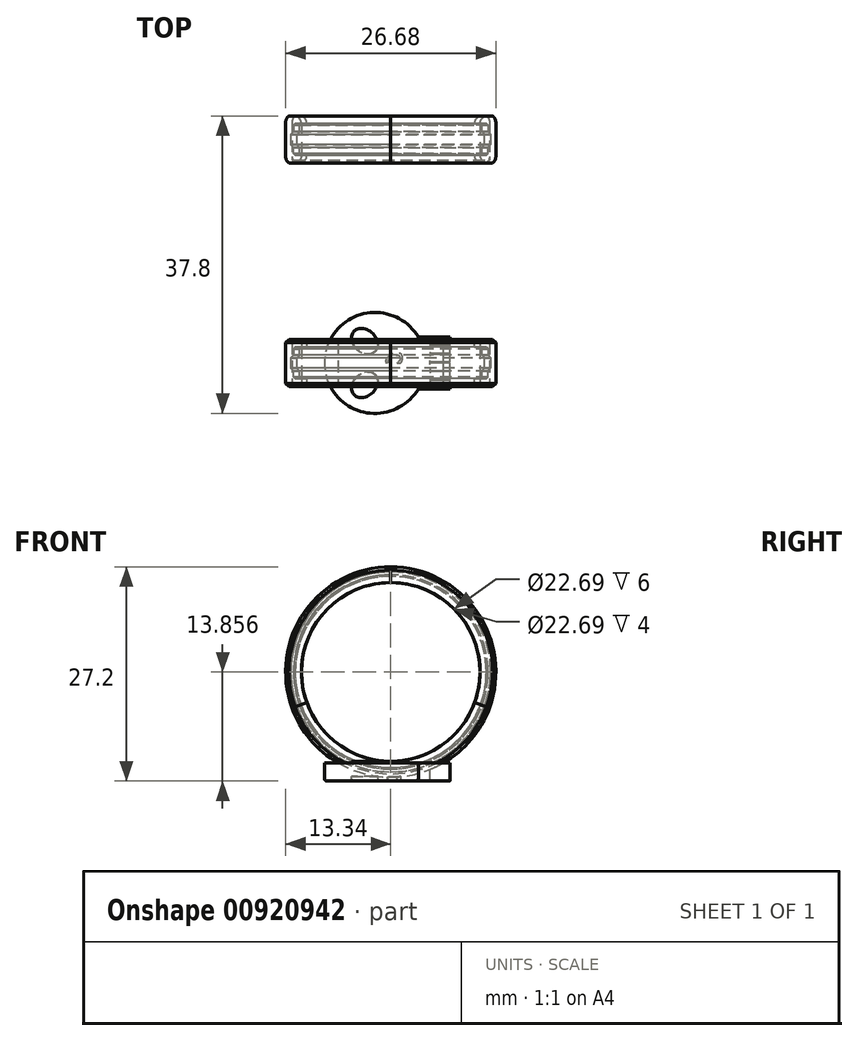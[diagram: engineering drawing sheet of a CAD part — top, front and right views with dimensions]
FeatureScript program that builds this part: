
annotation { "Feature Type Name" : "Feature", "Feature Type Description" : "" }
export const myFeature = defineFeature(function(context is Context, id is Id, definition is map)
    precondition{}
    {
        {
            var Q0;
            Q0=qCreatedBy(makeId("Right.planeOp"),FACE);
            var sketch = newSketch(context, id + "F0", { "sketchPlane" : qUnion([Q0])});
            skLineSegment(sketch, "E0", {"start": v(-19.63, -18.34) * mm, "end": v(80.37, -18.34) * mm, "construction": true});
            skLineSegment(sketch, "E1", {"start": v(-43.65, -18.34) * mm, "end": v(56.35, -18.34) * mm, "construction": true});
            skLineSegment(sketch, "E2.left", {"start": v(-31.4, -5.4) * mm, "end": v(-31.4, -7) * mm});
            skLineSegment(sketch, "E3", {"start": v(-30.2, -6) * mm, "end": v(-29.4, -6) * mm});
            skLineSegment(sketch, "E4", {"start": v(-27.4, -6) * mm, "end": v(-26.6, -6) * mm});
            skLineSegment(sketch, "E5", {"start": v(-29.4, -6) * mm, "end": v(-29.05, -5.65) * mm});
            skLineSegment(sketch, "E6", {"start": v(-27.4, -6) * mm, "end": v(-27.75, -5.65) * mm});
            skLineSegment(sketch, "E7", {"start": v(-30.4, -6.2) * mm, "end": v(-30.4, -7) * mm});
            skLineSegment(sketch, "E8", {"start": v(-26.4, -6.2) * mm, "end": v(-26.4, -7) * mm});
            skLineSegment(sketch, "E9", {"start": v(-31.4, -7) * mm, "end": v(-30.4, -7) * mm});
            skLineSegment(sketch, "E10", {"start": v(-26.4, -7) * mm, "end": v(-25.4, -7) * mm});
            skLineSegment(sketch, "E11", {"start": v(-30.4, -7) * mm, "end": v(-26.4, -7) * mm});
            skLineSegment(sketch, "E12", {"start": v(-29.05, -5.65) * mm, "end": v(-27.75, -5.65) * mm});
            skLineSegment(sketch, "E13", {"start": v(-25.4, -7) * mm, "end": v(-25.4, -5.4) * mm});
            skLineSegment(sketch, "E14", {"start": v(-25.8, -5) * mm, "end": v(-31, -5) * mm});
            skLineSegment(sketch, "E15", {"start": v(-31, -5) * mm, "end": v(-31.4, -5.4) * mm});
            skLineSegment(sketch, "E16", {"start": v(-25.4, -5.4) * mm, "end": v(-25.8, -5) * mm});
            skLineSegment(sketch, "E17", {"start": v(-30.4, -6.2) * mm, "end": v(-30.2, -6) * mm});
            skLineSegment(sketch, "E18", {"start": v(-26.4, -6.2) * mm, "end": v(-26.6, -6) * mm});
            skPoint(sketch, "E19.orphan", {"position": v(-31.4, -5) * mm});
            skPoint(sketch, "E20.orphan", {"position": v(-26.4, -6) * mm});
            skPoint(sketch, "E21.orphan", {"position": v(-30.4, -6) * mm});
            skLineSegment(sketch, "E22.left", {"start": v(-3.01, -5.4) * mm, "end": v(-3, -7) * mm});
            skLineSegment(sketch, "E23", {"start": v(-1.81, -6) * mm, "end": v(-1.01, -6) * mm});
            skLineSegment(sketch, "E24", {"start": v(1, -6) * mm, "end": v(1.8, -6) * mm});
            skLineSegment(sketch, "E25", {"start": v(-1.01, -6) * mm, "end": v(-0.66, -5.65) * mm});
            skLineSegment(sketch, "E26", {"start": v(1, -6) * mm, "end": v(0.64, -5.65) * mm});
            skLineSegment(sketch, "E27", {"start": v(-2.01, -6.2) * mm, "end": v(-2, -7) * mm});
            skLineSegment(sketch, "E28", {"start": v(2, -6.2) * mm, "end": v(2, -7) * mm});
            skLineSegment(sketch, "E29", {"start": v(-3, -7) * mm, "end": v(-2, -7) * mm});
            skLineSegment(sketch, "E30", {"start": v(2, -7) * mm, "end": v(3, -7) * mm});
            skLineSegment(sketch, "E31", {"start": v(-2, -7) * mm, "end": v(2, -7) * mm});
            skLineSegment(sketch, "E32", {"start": v(-0.66, -5.65) * mm, "end": v(0.64, -5.65) * mm});
            skLineSegment(sketch, "E33", {"start": v(3, -7) * mm, "end": v(3, -5.4) * mm});
            skLineSegment(sketch, "E34", {"start": v(2.6, -5) * mm, "end": v(-2.61, -5) * mm});
            skLineSegment(sketch, "E35", {"start": v(-2.61, -5) * mm, "end": v(-3.01, -5.4) * mm});
            skLineSegment(sketch, "E36", {"start": v(3, -5.4) * mm, "end": v(2.6, -5) * mm});
            skLineSegment(sketch, "E37", {"start": v(-2.01, -6.2) * mm, "end": v(-1.81, -6) * mm});
            skLineSegment(sketch, "E38", {"start": v(2, -6.2) * mm, "end": v(1.8, -6) * mm});
            skPoint(sketch, "E39.orphan", {"position": v(-3.01, -5) * mm});
            skPoint(sketch, "E40.orphan", {"position": v(2, -6) * mm});
            skPoint(sketch, "E41.orphan", {"position": v(-2.01, -6) * mm});
            skSolve(sketch);
        }
        {
            var Q0;
            Q0=makeQuery(id+"F0.imprint","IMPRINT",FACE,{"disambiguationData":[TD([[makeQuery(id+"F0.imprint","IMPRINT",EDGE,{"derivedFrom":sQuery(id+"F0.wireOp",EDGE,"E3")}),-1.0]])]});
            var Q1;
            Q1=makeQuery(id+"F0.imprint","IMPRINT",FACE,{"disambiguationData":[TD([[makeQuery(id+"F0.imprint","IMPRINT",EDGE,{"derivedFrom":sQuery(id+"F0.wireOp",EDGE,"E23")}),-1.0]])]});
            var Q2;
            Q2=sQuery(id+"F0.wireOp",EDGE,"E0");
            revolve(context, id + "F1", {"surfaceOperationType" : NewSurfaceOperationType.NEW, "entities" : qUnion([Q0, Q1]), "axis" : qUnion([Q2]), "revolveType" : RevolveType.FULL});
        }
        {
            var Q0;
            Q0=makeQuery(id+"F0.imprint","IMPRINT",FACE,{"disambiguationData":[TD([[makeQuery(id+"F0.imprint","IMPRINT",EDGE,{"derivedFrom":sQuery(id+"F0.wireOp",EDGE,"E2.left")}),1.0]])]});
            var Q1;
            Q1=makeQuery(id+"F0.imprint","IMPRINT",FACE,{"disambiguationData":[TD([[makeQuery(id+"F0.imprint","IMPRINT",EDGE,{"derivedFrom":sQuery(id+"F0.wireOp",EDGE,"E22.left")}),1.0]])]});
            var Q2;
            Q2=sQuery(id+"F0.wireOp",EDGE,"E0");
            revolve(context, id + "F2", {"surfaceOperationType" : NewSurfaceOperationType.NEW, "entities" : qUnion([Q0, Q1]), "axis" : qUnion([Q2]), "revolveType" : RevolveType.ONE_DIRECTION, "angle" : 110 * degree});
        }
        {
            var Q0;
            Q0=makeQuery(id+"F0.imprint","IMPRINT",FACE,{"disambiguationData":[TD([[makeQuery(id+"F0.imprint","IMPRINT",EDGE,{"derivedFrom":sQuery(id+"F0.wireOp",EDGE,"E2.left")}),1.0]])]});
            var Q1;
            Q1=makeQuery(id+"F0.imprint","IMPRINT",FACE,{"disambiguationData":[TD([[makeQuery(id+"F0.imprint","IMPRINT",EDGE,{"derivedFrom":sQuery(id+"F0.wireOp",EDGE,"E22.left")}),1.0]])]});
            var Q2;
            Q2=sQuery(id+"F0.wireOp",EDGE,"E0");
            revolve(context, id + "F3", {"surfaceOperationType" : NewSurfaceOperationType.NEW, "entities" : qUnion([Q0, Q1]), "axis" : qUnion([Q2]), "revolveType" : RevolveType.TWO_DIRECTIONS, "angle" : 250 * degree, "angleBack" : 110 * degree});
        }
        {
            var Q0;
            Q0=makeQuery(id+"F0.imprint","IMPRINT",FACE,{"disambiguationData":[TD([[makeQuery(id+"F0.imprint","IMPRINT",EDGE,{"derivedFrom":sQuery(id+"F0.wireOp",EDGE,"E2.left")}),1.0]])]});
            var Q1;
            Q1=makeQuery(id+"F0.imprint","IMPRINT",FACE,{"disambiguationData":[TD([[makeQuery(id+"F0.imprint","IMPRINT",EDGE,{"derivedFrom":sQuery(id+"F0.wireOp",EDGE,"E22.left")}),1.0]])]});
            var Q2;
            Q2=sQuery(id+"F0.wireOp",EDGE,"E0");
            revolve(context, id + "F4", {"surfaceOperationType" : NewSurfaceOperationType.NEW, "entities" : qUnion([Q0, Q1]), "axis" : qUnion([Q2]), "revolveType" : RevolveType.TWO_DIRECTIONS, "angle" : 360 * degree, "angleBack" : 250 * degree});
        }
        {
            var Q0;
            Q0=qCreatedBy(makeId("Top.planeOp"),FACE);
            var sketch = newSketch(context, id + "F5", { "sketchPlane" : qUnion([Q0])});
            skLineSegment(sketch, "E42.bottom", {"start": v(-7.5, -35.4) * mm, "end": v(7.5, -35.4) * mm, "construction": true});
            skLineSegment(sketch, "E42.top", {"start": v(-7.5, -21.4) * mm, "end": v(7.5, -21.4) * mm, "construction": true});
            skLineSegment(sketch, "E42.left", {"start": v(-7.5, -35.4) * mm, "end": v(-7.5, -21.4) * mm, "construction": true});
            skLineSegment(sketch, "E42.right", {"start": v(7.5, -35.4) * mm, "end": v(7.5, -30.65) * mm, "construction": true});
            skLineSegment(sketch, "E43", {"start": v(-7.5, -35.4) * mm, "end": v(3.5, -35.4) * mm, "construction": true});
            skLineSegment(sketch, "E44", {"start": v(-7.5, -21.4) * mm, "end": v(3.5, -21.4) * mm, "construction": true});
            skLineSegment(sketch, "E45", {"start": v(7.5, -35.4) * mm, "end": v(7.5, -31.7) * mm, "construction": true});
            skLineSegment(sketch, "E46", {"start": v(7.5, -21.4) * mm, "end": v(7.5, -25.1) * mm, "construction": true});
            skLineSegment(sketch, "E47", {"start": v(-7.5, -35.4) * mm, "end": v(-7.5, -31.7) * mm, "construction": true});
            skLineSegment(sketch, "E48", {"start": v(-7.5, -21.4) * mm, "end": v(-7.5, -25.1) * mm, "construction": true});
            skLineSegment(sketch, "E49", {"start": v(-7.5, -35.4) * mm, "end": v(-3.8, -35.4) * mm, "construction": true});
            skLineSegment(sketch, "E50", {"start": v(-7.5, -21.4) * mm, "end": v(-3.8, -21.4) * mm, "construction": true});
            skLineSegment(sketch, "E51", {"start": v(3.5, -35.4) * mm, "end": v(3.5, -31.7) * mm, "construction": true});
            skLineSegment(sketch, "E52", {"start": v(3.5, -21.4) * mm, "end": v(3.5, -25.1) * mm, "construction": true});
            skArc(sketch, "E53", {"start": v(3.5, -25.1) * mm, "mid": v(-8.41, -28.4) * mm, "end": v(3.5, -31.7) * mm});
            skLineSegment(sketch, "E54.bottom", {"start": v(7.5, -31.7) * mm, "end": v(3.5, -31.7) * mm});
            skLineSegment(sketch, "E54.top", {"start": v(7.5, -25.1) * mm, "end": v(3.5, -25.1) * mm});
            skLineSegment(sketch, "E54.left", {"start": v(7.5, -31.7) * mm, "end": v(7.5, -30.65) * mm});
            skLineSegment(sketch, "E55", {"start": v(-2, -28.4) * mm, "end": v(14.58, -28.4) * mm, "construction": true});
            skLineSegment(sketch, "E56", {"start": v(-2, -28.4) * mm, "end": v(-16.13, -28.4) * mm, "construction": true});
            skLineSegment(sketch, "E57", {"start": v(7.5, -31.7) * mm, "end": v(7.5, -30.65) * mm, "construction": true});
            skLineSegment(sketch, "E58", {"start": v(7.5, -25.1) * mm, "end": v(7.5, -26.1) * mm, "construction": true});
            skLineSegment(sketch, "E59", {"start": v(7.5, -26.2) * mm, "end": v(7.5, -27.2) * mm, "construction": true});
            skLineSegment(sketch, "E60", {"start": v(7.5, -27.3) * mm, "end": v(7.5, -28.3) * mm, "construction": true});
            skLineSegment(sketch, "E61", {"start": v(7.5, -28.4) * mm, "end": v(7.5, -29.4) * mm, "construction": true});
            skLineSegment(sketch, "E62", {"start": v(7.5, -29.5) * mm, "end": v(7.5, -30.55) * mm, "construction": true});
            skLineSegment(sketch, "E63", {"start": v(7.5, -30.65) * mm, "end": v(5, -30.65) * mm, "construction": true});
            skLineSegment(sketch, "E64", {"start": v(7.5, -30.55) * mm, "end": v(5, -30.55) * mm, "construction": true});
            skLineSegment(sketch, "E65", {"start": v(7.5, -29.5) * mm, "end": v(5, -29.5) * mm, "construction": true});
            skLineSegment(sketch, "E66", {"start": v(7.5, -29.4) * mm, "end": v(5, -29.4) * mm, "construction": true});
            skLineSegment(sketch, "E67", {"start": v(7.5, -28.4) * mm, "end": v(5, -28.4) * mm, "construction": true});
            skLineSegment(sketch, "E68", {"start": v(7.5, -28.3) * mm, "end": v(5, -28.3) * mm, "construction": true});
            skLineSegment(sketch, "E69", {"start": v(7.5, -27.3) * mm, "end": v(5, -27.3) * mm, "construction": true});
            skLineSegment(sketch, "E70", {"start": v(7.5, -27.2) * mm, "end": v(5, -27.2) * mm, "construction": true});
            skLineSegment(sketch, "E71", {"start": v(7.5, -26.2) * mm, "end": v(5, -26.2) * mm, "construction": true});
            skLineSegment(sketch, "E72", {"start": v(7.5, -26.1) * mm, "end": v(5, -26.1) * mm, "construction": true});
            skLineSegment(sketch, "E73", {"start": v(7.5, -25.1) * mm, "end": v(5, -25.1) * mm, "construction": true});
            skLineSegment(sketch, "E74.bottom", {"start": v(7.5, -31.7) * mm, "end": v(5, -31.7) * mm});
            skLineSegment(sketch, "E74.top", {"start": v(7.5, -30.65) * mm, "end": v(5, -30.65) * mm});
            skLineSegment(sketch, "E75.bottom", {"start": v(7.5, -30.55) * mm, "end": v(5, -30.55) * mm});
            skLineSegment(sketch, "E75.top", {"start": v(7.5, -29.5) * mm, "end": v(5, -29.5) * mm});
            skLineSegment(sketch, "E75.left", {"start": v(7.5, -30.55) * mm, "end": v(7.5, -29.5) * mm});
            skLineSegment(sketch, "E76.bottom", {"start": v(7.5, -29.4) * mm, "end": v(5, -29.4) * mm});
            skLineSegment(sketch, "E76.top", {"start": v(7.5, -28.4) * mm, "end": v(5, -28.4) * mm});
            skLineSegment(sketch, "E76.left", {"start": v(7.5, -29.4) * mm, "end": v(7.5, -28.4) * mm});
            skLineSegment(sketch, "E77.bottom", {"start": v(7.5, -28.3) * mm, "end": v(5, -28.3) * mm});
            skLineSegment(sketch, "E77.top", {"start": v(7.5, -27.3) * mm, "end": v(5, -27.3) * mm});
            skLineSegment(sketch, "E77.left", {"start": v(7.5, -28.3) * mm, "end": v(7.5, -27.3) * mm});
            skLineSegment(sketch, "E78.bottom", {"start": v(7.5, -27.2) * mm, "end": v(5, -27.2) * mm});
            skLineSegment(sketch, "E78.top", {"start": v(7.5, -26.2) * mm, "end": v(5, -26.2) * mm});
            skLineSegment(sketch, "E78.left", {"start": v(7.5, -27.2) * mm, "end": v(7.5, -26.2) * mm});
            skLineSegment(sketch, "E79.bottom", {"start": v(7.5, -26.1) * mm, "end": v(5, -26.1) * mm});
            skLineSegment(sketch, "E79.top", {"start": v(7.5, -25.1) * mm, "end": v(5, -25.1) * mm});
            skLineSegment(sketch, "E79.left", {"start": v(7.5, -26.1) * mm, "end": v(7.5, -25.1) * mm});
            skLineSegment(sketch, "E80.trimOffspring", {"start": v(7.5, -26.1) * mm, "end": v(7.5, -21.4) * mm, "construction": true});
            skLineSegment(sketch, "E81.trimOffspring", {"start": v(7.5, -27.2) * mm, "end": v(7.5, -26.2) * mm, "construction": true});
            skLineSegment(sketch, "E82.trimOffspring", {"start": v(7.5, -28.3) * mm, "end": v(7.5, -27.3) * mm, "construction": true});
            skLineSegment(sketch, "E83.trimOffspring", {"start": v(7.5, -29.4) * mm, "end": v(7.5, -28.4) * mm, "construction": true});
            skLineSegment(sketch, "E84", {"start": v(5, -26.1) * mm, "end": v(5, -26.2) * mm});
            skLineSegment(sketch, "E85", {"start": v(5, -27.2) * mm, "end": v(5, -27.3) * mm});
            skLineSegment(sketch, "E86", {"start": v(5, -28.4) * mm, "end": v(5, -28.3) * mm});
            skLineSegment(sketch, "E87", {"start": v(5, -29.4) * mm, "end": v(5, -29.5) * mm});
            skLineSegment(sketch, "E88", {"start": v(5, -30.55) * mm, "end": v(5, -30.65) * mm});
            skEllipse(sketch, "E89", {"center": v(-3.32, -31.16) * mm, "majorRadius": 1.86 * mm, "minorRadius": 1.43 * mm, "majorAxis": v(0.75, 0.66)});
            skEllipse(sketch, "E90.MirrorC", {"center": v(-3.32, -25.64) * mm, "majorRadius": 1.86 * mm, "minorRadius": 1.43 * mm, "majorAxis": v(0.75, -0.66)});
            skEllipticalArc(sketch, "E91", {});
            skEllipticalArc(sketch, "E92.MirrorC", {});
            const initialGuessF5  = {"E91": [0.00041814075666479766, -0.028739335015416145, 0.8598697694904957, -0.5105134469496, 0.0008899998552671086, 0.0005061024959400816, 3.3790587946130737, 1.3764349525376756], "E92.MirrorC": [0.00041814075666479766, -0.028060867405582515, 0.8598697694904957, 0.5105134469496, 0.0008899998552671086, 0.0005061024959400816, 4.906750354641911, 2.9041265125665126]};
            skSetInitialGuess(sketch, initialGuessF5);
            skSolve(sketch);
        }
        {
            var Q0;
            Q0=makeQuery(id+"F5.imprint","IMPRINT",FACE,{"disambiguationData":[TD([[makeQuery(id+"F5.imprint","IMPRINT",EDGE,{"derivedFrom":sQuery(id+"F5.wireOp",EDGE,"E53")}),1.0]])]});
            var Q1;
            Q1=makeQuery(id+"F3.opRevolve","SWEPT_FACE",FACE,{"disambiguationData":[OSD([sQuery(id+"F0.wireOp",EDGE,"E14")])]});
            var Q2;
            Q2=makeQuery(id+"F3.opRevolve","SWEPT_BODY",BODY,{"disambiguationData":[OSD([sQuery(id+"F0.wireOp",EDGE,"E2.left"),sQuery(id+"F0.wireOp",EDGE,"E3"),sQuery(id+"F0.wireOp",EDGE,"E4"),sQuery(id+"F0.wireOp",EDGE,"E5"),sQuery(id+"F0.wireOp",EDGE,"E6"),sQuery(id+"F0.wireOp",EDGE,"E7"),sQuery(id+"F0.wireOp",EDGE,"E8"),sQuery(id+"F0.wireOp",EDGE,"E9"),sQuery(id+"F0.wireOp",EDGE,"E10"),sQuery(id+"F0.wireOp",EDGE,"E12"),sQuery(id+"F0.wireOp",EDGE,"E13"),sQuery(id+"F0.wireOp",EDGE,"E14"),sQuery(id+"F0.wireOp",EDGE,"E15"),sQuery(id+"F0.wireOp",EDGE,"E16"),sQuery(id+"F0.wireOp",EDGE,"E17"),sQuery(id+"F0.wireOp",EDGE,"E18")])]});
            var Q3;
            Q3=makeQuery(id+"F3.opRevolve","SWEPT_FACE",FACE,{"disambiguationData":[OSD([sQuery(id+"F0.wireOp",EDGE,"E14")])]});
            extrude(context, id + "F6", {"entities" : qUnion([Q0]), "operationType" : NewBodyOperationType.ADD, "oppositeDirection" : true, "depth" : 32.2 * mm, "endBoundEntityFace" : qUnion([Q1]), "endBoundEntityBody" : qUnion([Q2]), "hasOffset" : true, "offsetDistance" : 21 * mm, "offsetOppositeDirection" : true, "hasSecondDirection" : true, "secondDirectionOppositeDirection" : true, "secondDirectionDepth" : 29.9 * mm, "secondDirectionBoundEntityFace" : qUnion([Q3]), "hasSecondDirectionOffset" : true, "secondDirectionOffsetDistance" : 10 * mm});
        }
        {
            var Q0;
            Q0=makeQuery(id+"F5.imprint","IMPRINT",FACE,{"disambiguationData":[TD([[makeQuery(id+"F5.imprint","IMPRINT",EDGE,{"derivedFrom":sQuery(id+"F5.wireOp",EDGE,"E90.MirrorC")}),1.0]])]});
            var Q1;
            Q1=makeQuery(id+"F5.imprint","IMPRINT",FACE,{"disambiguationData":[TD([[makeQuery(id+"F5.imprint","IMPRINT",EDGE,{"derivedFrom":sQuery(id+"F5.wireOp",EDGE,"E89")}),1.0]])]});
            extrude(context, id + "F7", {"entities" : qUnion([Q0, Q1]), "operationType" : NewBodyOperationType.ADD, "oppositeDirection" : true, "depth" : 31.6 * mm, "offsetDistance" : 25 * mm, "hasSecondDirection" : true, "secondDirectionOppositeDirection" : true, "secondDirectionDepth" : 29.7 * mm});
        }
        {
            var Q0;
            Q0=makeQuery(id+"F6.opExtrude","CAP_EDGE",EDGE,{"disambiguationData":[OSD([sQuery(id+"F5.wireOp",EDGE,"E54.top"),sQuery(id+"F5.wireOp",EDGE,"E79.top")])],"isStart":false});
            var Q1;
            Q1=makeQuery(id+"F6.opExtrude","CAP_EDGE",EDGE,{"disambiguationData":[OSD([sQuery(id+"F5.wireOp",EDGE,"E54.bottom"),sQuery(id+"F5.wireOp",EDGE,"E74.bottom")])],"isStart":false});
            var Q2;
            Q2=makeQuery(id+"F6.opExtrude","CAP_EDGE",EDGE,{"disambiguationData":[OSD([sQuery(id+"F5.wireOp",EDGE,"E75.bottom")])],"isStart":false});
            var Q3;
            Q3=makeQuery(id+"F6.opExtrude","CAP_EDGE",EDGE,{"disambiguationData":[OSD([sQuery(id+"F5.wireOp",EDGE,"E74.top")])],"isStart":false});
            var Q4;
            Q4=makeQuery(id+"F6.opExtrude","CAP_EDGE",EDGE,{"disambiguationData":[OSD([sQuery(id+"F5.wireOp",EDGE,"E75.top")])],"isStart":false});
            var Q5;
            Q5=makeQuery(id+"F6.opExtrude","CAP_EDGE",EDGE,{"disambiguationData":[OSD([sQuery(id+"F5.wireOp",EDGE,"E76.bottom")])],"isStart":false});
            var Q6;
            Q6=makeQuery(id+"F6.opExtrude","CAP_EDGE",EDGE,{"disambiguationData":[OSD([sQuery(id+"F5.wireOp",EDGE,"E76.top")])],"isStart":false});
            var Q7;
            Q7=makeQuery(id+"F6.opExtrude","CAP_EDGE",EDGE,{"disambiguationData":[OSD([sQuery(id+"F5.wireOp",EDGE,"E77.bottom")])],"isStart":false});
            var Q8;
            Q8=makeQuery(id+"F6.opExtrude","CAP_EDGE",EDGE,{"disambiguationData":[OSD([sQuery(id+"F5.wireOp",EDGE,"E77.top")])],"isStart":false});
            var Q9;
            Q9=makeQuery(id+"F6.opExtrude","CAP_EDGE",EDGE,{"disambiguationData":[OSD([sQuery(id+"F5.wireOp",EDGE,"E78.bottom")])],"isStart":false});
            var Q10;
            Q10=makeQuery(id+"F6.opExtrude","CAP_EDGE",EDGE,{"disambiguationData":[OSD([sQuery(id+"F5.wireOp",EDGE,"E78.top")])],"isStart":false});
            var Q11;
            Q11=makeQuery(id+"F6.opExtrude","CAP_EDGE",EDGE,{"disambiguationData":[OSD([sQuery(id+"F5.wireOp",EDGE,"E79.bottom")])],"isStart":false});
            fillet(context, id + "F8", {"entities" : qUnion([Q0, Q1, Q2, Q3, Q4, Q5, Q6, Q7, Q8, Q9, Q10, Q11]), "radius" : 0.2 * mm, "tangentPropagation" : true, "allowEdgeOverflow" : false});
        }
        {
            var Q0;
            Q0=makeQuery(id+"F6.opExtrude","CAP_EDGE",EDGE,{"disambiguationData":[OSD([sQuery(id+"F5.wireOp",EDGE,"E53")])],"isStart":false});
            var Q1;
            Q1=makeQuery(id+"F6.opExtrude","CAP_EDGE",EDGE,{"disambiguationData":[OSD([sQuery(id+"F5.wireOp",EDGE,"E90.MirrorC")])],"isStart":false});
            var Q2;
            Q2=makeQuery(id+"F6.opExtrude","CAP_EDGE",EDGE,{"disambiguationData":[OSD([sQuery(id+"F5.wireOp",EDGE,"E89")])],"isStart":false});
            var Q3;
            Q3=makeQuery(id+"F6.opExtrude","CAP_EDGE",EDGE,{"disambiguationData":[OSD([sQuery(id+"F5.wireOp",EDGE,"E92.MirrorC")])],"isStart":false});
            var Q4;
            Q4=makeQuery(id+"F6.opExtrude","CAP_EDGE",EDGE,{"disambiguationData":[OSD([sQuery(id+"F5.wireOp",EDGE,"E91")])],"isStart":false});
            fillet(context, id + "F9", {"entities" : qUnion([Q0, Q1, Q2, Q3, Q4]), "radius" : 0.3 * mm, "tangentPropagation" : true, "allowEdgeOverflow" : false});
        }
        {
            var Q0;
            Q0=makeQuery(id+"F2.opRevolve","SWEPT_EDGE",EDGE,{"disambiguationData":[OSD([sQuery(id+"F0.wireOp",EDGE,"E34"),sQuery(id+"F0.wireOp",EDGE,"E35")])]});
            var Q1;
            Q1=makeQuery(id+"F4.opRevolve","SWEPT_EDGE",EDGE,{"disambiguationData":[OSD([sQuery(id+"F0.wireOp",EDGE,"E34"),sQuery(id+"F0.wireOp",EDGE,"E35")])]});
            var Q2;
            Q2=makeQuery(id+"F3.opRevolve","SWEPT_EDGE",EDGE,{"disambiguationData":[OSD([sQuery(id+"F0.wireOp",EDGE,"E22.left"),sQuery(id+"F0.wireOp",EDGE,"E29")])]});
            var Q3;
            Q3=makeQuery(id+"F3.opRevolve","SWEPT_EDGE",EDGE,{"disambiguationData":[OSD([sQuery(id+"F0.wireOp",EDGE,"E30"),sQuery(id+"F0.wireOp",EDGE,"E33")])]});
            var Q4;
            Q4=makeQuery(id+"F4.opRevolve","SWEPT_EDGE",EDGE,{"disambiguationData":[OSD([sQuery(id+"F0.wireOp",EDGE,"E22.left"),sQuery(id+"F0.wireOp",EDGE,"E29")])]});
            var Q5;
            Q5=makeQuery(id+"F2.opRevolve","SWEPT_EDGE",EDGE,{"disambiguationData":[OSD([sQuery(id+"F0.wireOp",EDGE,"E22.left"),sQuery(id+"F0.wireOp",EDGE,"E29")])]});
            var Q6;
            Q6=makeQuery(id+"F2.opRevolve","SWEPT_EDGE",EDGE,{"disambiguationData":[OSD([sQuery(id+"F0.wireOp",EDGE,"E30"),sQuery(id+"F0.wireOp",EDGE,"E33")])]});
            var Q7;
            Q7=makeQuery(id+"F3.opRevolve","SWEPT_EDGE",EDGE,{"disambiguationData":[OSD([sQuery(id+"F0.wireOp",EDGE,"E22.left"),sQuery(id+"F0.wireOp",EDGE,"E35")])]});
            var Q8;
            Q8=makeQuery(id+"F4.opRevolve","SWEPT_EDGE",EDGE,{"disambiguationData":[OSD([sQuery(id+"F0.wireOp",EDGE,"E30"),sQuery(id+"F0.wireOp",EDGE,"E33")])]});
            var Q9;
            Q9=makeQuery(id+"F4.opRevolve","SWEPT_EDGE",EDGE,{"disambiguationData":[OSD([sQuery(id+"F0.wireOp",EDGE,"E34"),sQuery(id+"F0.wireOp",EDGE,"E36")])]});
            var Q10;
            Q10=makeQuery(id+"F2.opRevolve","SWEPT_EDGE",EDGE,{"disambiguationData":[OSD([sQuery(id+"F0.wireOp",EDGE,"E34"),sQuery(id+"F0.wireOp",EDGE,"E36")])]});
            var Q11;
            Q11=makeQuery(id+"F3.opRevolve","SWEPT_EDGE",EDGE,{"disambiguationData":[OSD([sQuery(id+"F0.wireOp",EDGE,"E34"),sQuery(id+"F0.wireOp",EDGE,"E36")])]});
            fillet(context, id + "F10", {"entities" : qUnion([Q0, Q1, Q2, Q3, Q4, Q5, Q6, Q7, Q8, Q9, Q10, Q11]), "radius" : 1 * mm, "tangentPropagation" : true, "allowEdgeOverflow" : false});
        }
    });
